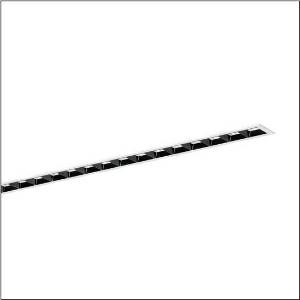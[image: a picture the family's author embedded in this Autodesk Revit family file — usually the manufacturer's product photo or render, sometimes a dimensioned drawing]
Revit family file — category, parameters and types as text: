
# Revit family: silica_r__21_51mx12db35wb_b505
name_source: partatom
category: Lighting Fixtures
units: mm (PartAtom-declared; Revit-internal decimal feet)

## family parameters
Cut with Voids When Loaded = No
Host = Face
Light Source = No
Part Type = Normal
Room Calculation Point = No
Round Connector Dimension = Use Diameter
Shared = No

## types (1)
- --- (1 x LED, 5400 lm, 34.3 W, 3000K)
    Apparent Load = 34 VA
    CIE Flux Codes = 86 100 100 100 100
    Color Rendering = 80
    Color Temperature = 3000K
    Default Elevation = 1800 mm
    Description = Silica® 21, office luminaire, primary light control with darklight reflector, of PMMA, black, CAT 2 (L<= 3000cd/m²), light emission: direct distribution, primary light characteristic: symmetric, installation type: recessed, LED, rated luminous flux: 5.400lm, luminous efficacy: 157lm/W, light colour: 830, colour temperature: 3000K, with terminal, 3+2-pole, max. 2.5mm², mains connection: 220..240V, AC, 50/60Hz, rated input power: 34.3W, luminaire housing, of aluminium, traffic white (RAL 9016), length: 1.528mm, width: 79mm, height: 53mm, protection rating (complete): IP20, insulation class (complete): insulation class I (protective earthing), certification: CE, permissible operating ambient temperature: 0..+35°C, standard: EN 50419, packaging unit: 1 piece
    Height = 0 mm  [stored 0 ft]
    Lamp = 1 x LED
    Lamp Light Flux = 5400 lm
    Lamp Power = 34.3 W
    Lamp count = 1
    Length = 1527 mm
    Luminous efficacy = 157 lm/W
    Manufacturer = Siteco
    ModVariant = No
    Model = 51MX12DB35WB
    Mounting Place = Ceiling
    Mounting Type = Recessed
    Number of Poles = 1
    OnlyDefault = Yes
    Power Factor = 1
    Product Name = Silica® 21
    Product group = office luminaire | ceiling recessed
    ProductGroupID = 400
    Protection Class = Protection class I
    Protection Degree = IP 20
    RLX_Detail_Level = 1
    RlxData = <blob elided: 42009 chars, md5=2966f600>
    Socket = socket
    Standby Power = 0 W
    System Light Flux = 5400 lm
    System Power = 34 W
    Type Comments = factory setting: luminous flux: 100 % | dim-lin: 254 | 392 mA
    Type Image = l_1251632.jpg
    URL = http://relux.com
    VarID = @adj_034109
    Voltage = 0 V
    Weight = 0.00 kg
    Width = 79 mm

note: [stored X ft] marks values corroborated as IEEE doubles in the binary element streams (Revit-internal decimal feet)

## geometry (parser evidence)
native form markers: Blend x4, Sweep x10
no freeform markers — native parametric forms only
